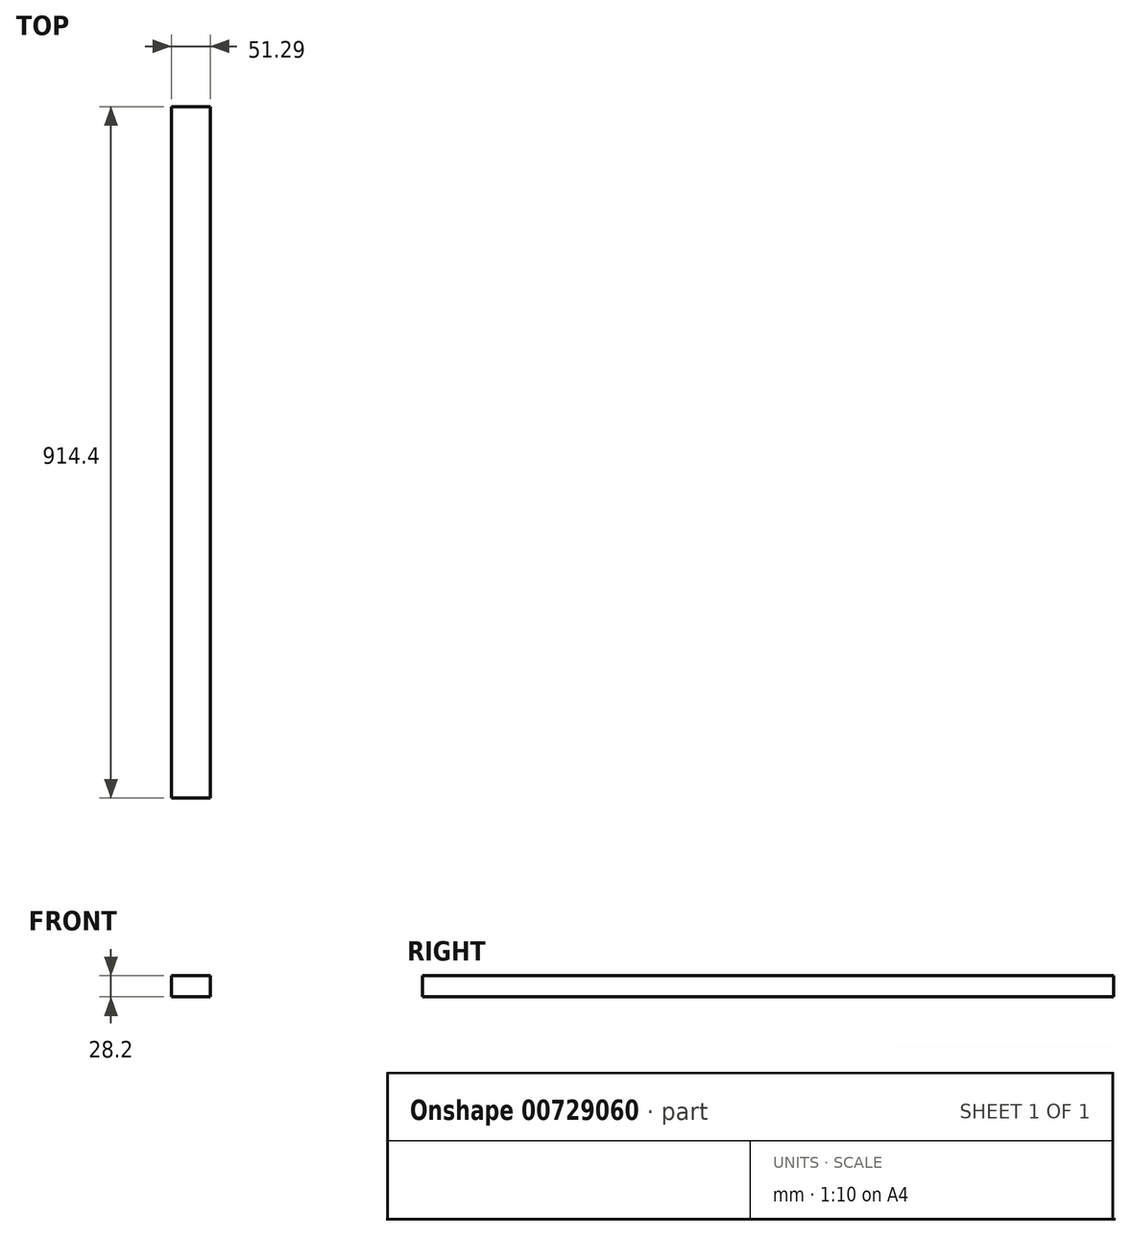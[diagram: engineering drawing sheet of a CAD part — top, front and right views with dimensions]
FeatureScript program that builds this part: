
annotation { "Feature Type Name" : "Feature", "Feature Type Description" : "" }
export const myFeature = defineFeature(function(context is Context, id is Id, definition is map)
    precondition{}
    {
        {
            var Q0;
            Q0=qCreatedBy(makeId("Front.planeOp"),FACE);
            var sketch = newSketch(context, id + "F0", { "sketchPlane" : qUnion([Q0])});
            skLineSegment(sketch, "E0.bottom", {"start": v(0, 0) * mm, "end": v(51.3, 0) * mm});
            skLineSegment(sketch, "E0.top", {"start": v(0, 28.2) * mm, "end": v(51.3, 28.2) * mm});
            skLineSegment(sketch, "E0.left", {"start": v(0, 0) * mm, "end": v(0, 28.2) * mm});
            skLineSegment(sketch, "E0.right", {"start": v(51.3, 0) * mm, "end": v(51.3, 28.2) * mm});
            skSolve(sketch);
        }
        {
            var Q0;
            Q0=makeQuery(id+"F0.imprint","IMPRINT",FACE,{"disambiguationData":[TD([[makeQuery(id+"F0.imprint","IMPRINT",EDGE,{"derivedFrom":sQuery(id+"F0.wireOp",EDGE,"E0.bottom")}),1.0]])]});
            extrude(context, id + "F1", {"entities" : qUnion([Q0]), "depth" : 914.4 * mm, "offsetDistance" : 25.4 * mm});
        }
    });
